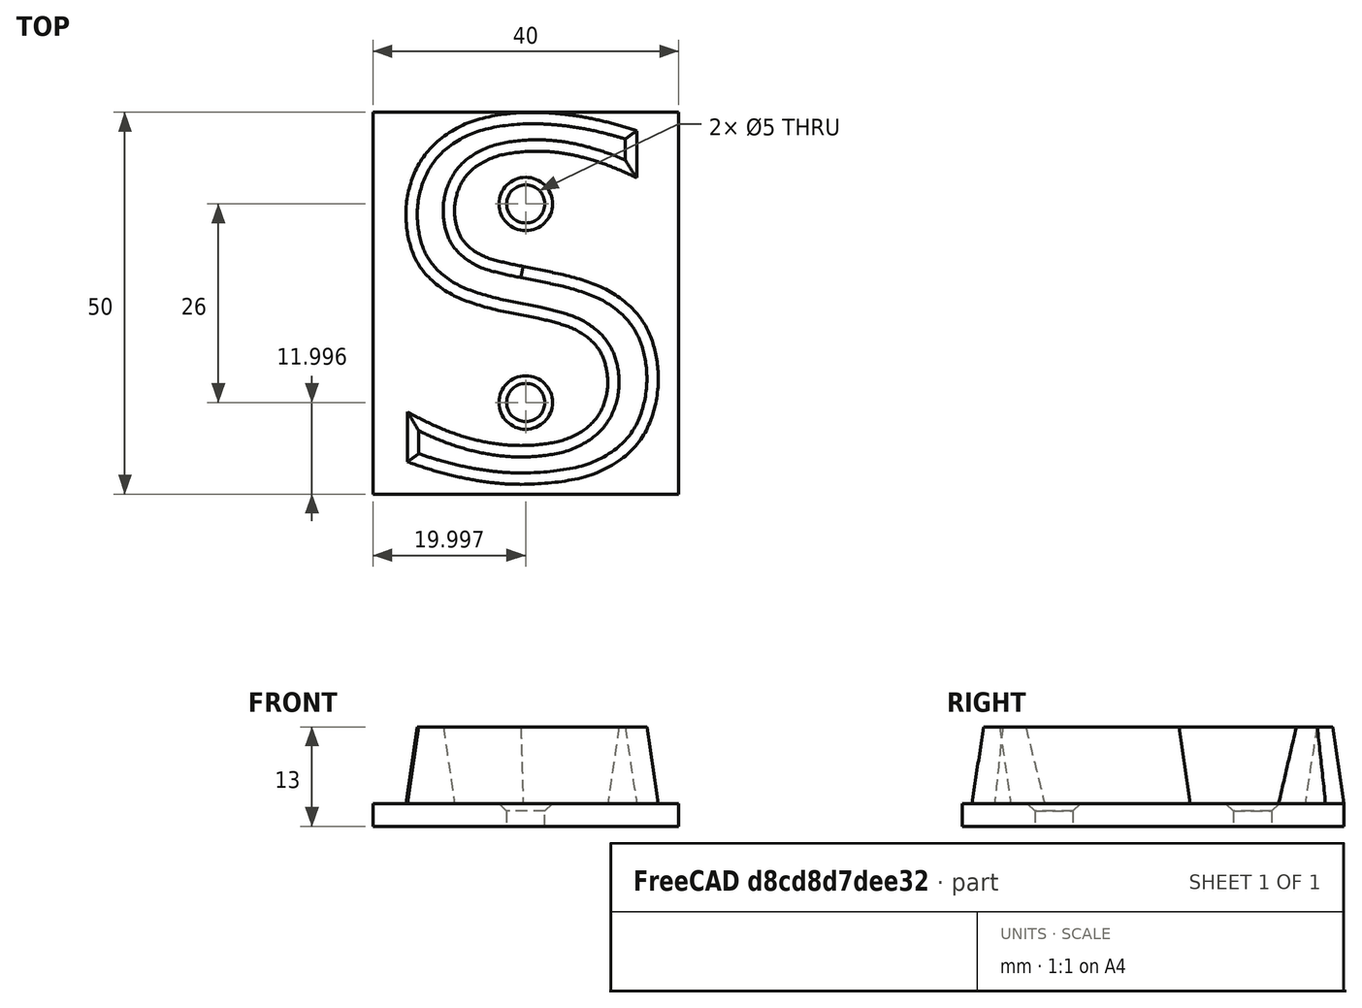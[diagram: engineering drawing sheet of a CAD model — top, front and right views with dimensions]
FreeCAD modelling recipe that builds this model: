
FCSTD DOCUMENT  (FreeCAD 0.21RUnknown)
Label: s_cb3_mounting_holes
License: All rights reserved
LicenseURL: https://en.wikipedia.org/wiki/All_rights_reserved
objects: Part::Part2DObjectPython×3, Part::Extrusion×3, Part::Feature×3, Part::Offset2D×2, Part::Cut×2, Part::Loft×1, Part::Chamfer×1
note: 15 computed .brp shape members not serialized (recipe doc carries the construction recipe); baked Part::Feature solids carry a one-line shape summary decoded from their .brp

FEATURE [Part::Part2DObjectPython] Rectangle  # Draft 2D object (typed FeaturePython)
  Area = 2000
  ChamferSize = 0
  Columns = 1
  FilletRadius = 0
  Height = 50
  Length = 40
  MakeFace = true
  Placement = pos=(-0.0534207,-0.213677,2) rot=(0,0,1;0rad)
  Rows = 1
FEATURE [Part::Extrusion] Extrusion
  Base = -> Rectangle
  Dir = (0,0,3)
  DirMode = 0
  FaceMakerClass = Part::FaceMakerBullseye
  LengthFwd = 0
  LengthRev = 0
  Solid = true
  Symmetric = false
FEATURE [Part::Feature] Wire
  shape: bbox 30.23 x 43.62 x 2e-07 mm, 0 faces, 0 solids (baked)
FEATURE [Part::Feature] Wire001
  shape: bbox 32.88 x 43.62 x 2e-07 mm, 0 faces, 0 solids (baked)
FEATURE [Part::Feature] Wire002
  shape: bbox 33.06 x 48.72 x 2e-07 mm, 0 faces, 0 solids (baked)
FEATURE [Part::Offset2D] Offset2D
  Fill = false
  Intersection = false
  Join = 0
  Mode = 1
  Placement = pos=(0,0,10) rot=(0,0,1;0rad)
  SelfIntersection = false
  Source = -> Wire002
  Value = -1.5
FEATURE [Part::Offset2D] Offset2D001
  Fill = false
  Intersection = false
  Join = 0
  Mode = 1
  SelfIntersection = false
  Source = -> Wire002
  Value = -0.01
FEATURE [Part::Loft] Loft
  Closed = false
  MaxDegree = 5
  Ruled = true
  Sections = -> [Offset2D,Offset2D001]
  Solid = true
FEATURE [Part::Part2DObjectPython] Circle  # Draft 2D object (typed FeaturePython)
  Area = 19.635
  FirstAngle = 0
  LastAngle = 0
  MakeFace = true
  Placement = pos=(19.9466,37.7863,0) rot=(0,0,1;0rad)
  Radius = 2.5
FEATURE [Part::Extrusion] Extrude
  Base = -> Circle
  Dir = (0,0,1)
  DirMode = 2
  FaceMakerClass = Part::FaceMakerBullseye
  LengthFwd = 10
  LengthRev = 0
  Solid = true
  Symmetric = false
FEATURE [Part::Cut] Cut
  Base = -> Extrusion
  Tool = -> Extrude
FEATURE [Part::Part2DObjectPython] Circle001  # Draft 2D object (typed FeaturePython)
  Area = 19.635
  FirstAngle = 0
  LastAngle = 0
  MakeFace = true
  Placement = pos=(19.9466,11.7863,0) rot=(0,0,1;0rad)
  Radius = 2.5
FEATURE [Part::Extrusion] Extrude001
  Base = -> Circle001
  Dir = (0,0,1)
  DirMode = 2
  FaceMakerClass = Part::FaceMakerBullseye
  LengthFwd = 10
  LengthRev = 0
  Solid = true
  Symmetric = false
FEATURE [Part::Cut] Cut001
  Base = -> Cut
  Tool = -> Extrude001
FEATURE [Part::Chamfer] Chamfer
  Base = -> Cut001
  Edges = 2 edges r=1: [Edge15,Edge16]
